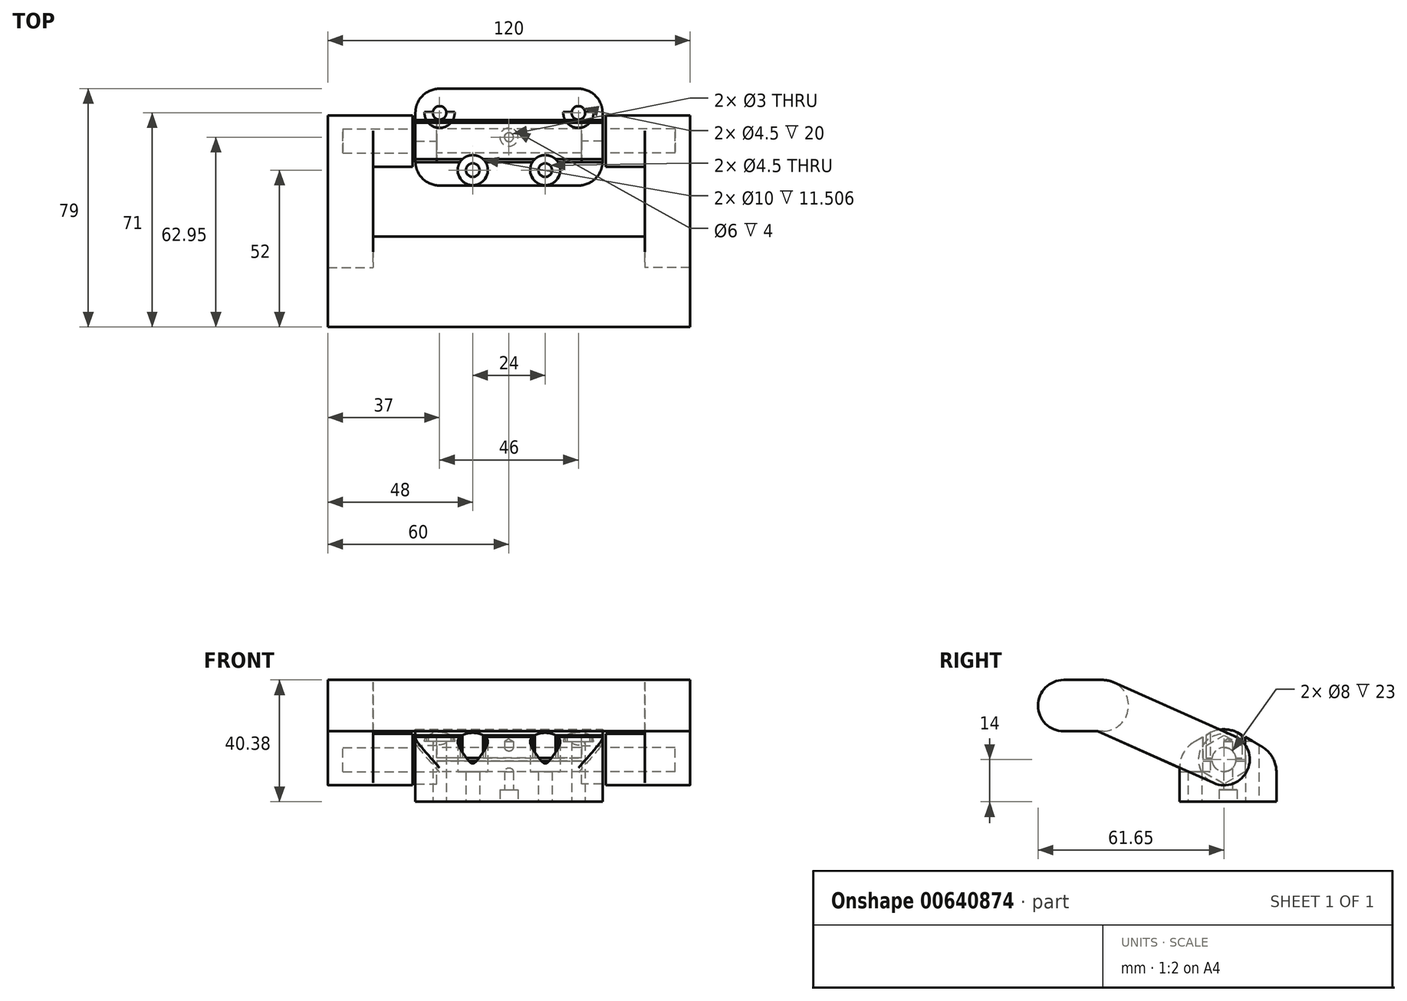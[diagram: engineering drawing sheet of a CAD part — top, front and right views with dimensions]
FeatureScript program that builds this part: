
annotation { "Feature Type Name" : "Feature", "Feature Type Description" : "" }
export const myFeature = defineFeature(function(context is Context, id is Id, definition is map)
    precondition{}
    {
        {
            var Q0;
            Q0=qCreatedBy(makeId("Top.planeOp"),FACE);
            var sketch = newSketch(context, id + "F0", { "sketchPlane" : qUnion([Q0])});
            skLineSegment(sketch, "E0.top", {"start": v(-31, -41) * mm, "end": v(31, -41) * mm, "construction": true});
            skLineSegment(sketch, "E0.left", {"start": v(-31, 41) * mm, "end": v(-31, -41) * mm, "construction": true});
            skLineSegment(sketch, "E0.right", {"start": v(31, 41) * mm, "end": v(31, -41) * mm, "construction": true});
            skPoint(sketch, "E0.middle", {"position": v(0, 0) * mm});
            skCircle(sketch, "E1", {"center": v(-23, 30) * mm, "radius": 2.25 * mm});
            skCircle(sketch, "E2", {"center": v(23, 30) * mm, "radius": 2.25 * mm});
            skCircle(sketch, "E3", {"center": v(-12, 11) * mm, "radius": 2.25 * mm});
            skCircle(sketch, "E4", {"center": v(12, 11) * mm, "radius": 2.25 * mm});
            skArc(sketch, "E5", {"start": v(-23, 38) * mm, "mid": v(-28.66, 35.66) * mm, "end": v(-31, 30) * mm});
            skArc(sketch, "E6", {"start": v(31, 30) * mm, "mid": v(28.66, 35.66) * mm, "end": v(23, 38) * mm});
            skCircle(sketch, "E7", {"center": v(12, 11) * mm, "radius": 5 * mm});
            skCircle(sketch, "E8", {"center": v(-12, 11) * mm, "radius": 5 * mm});
            skLineSegment(sketch, "E9", {"start": v(0, 41) * mm, "end": v(0, -41) * mm, "construction": true});
            skLineSegment(sketch, "E10", {"start": v(-31, 41) * mm, "end": v(31, 41) * mm, "construction": true});
            skLineSegment(sketch, "E11", {"start": v(-31, 38) * mm, "end": v(31, 38) * mm, "construction": true});
            skLineSegment(sketch, "E12", {"start": v(-23, 38) * mm, "end": v(23, 38) * mm});
            skLineSegment(sketch, "E13", {"start": v(23, 5.9) * mm, "end": v(-23, 5.9) * mm});
            skLineSegment(sketch, "E14", {"start": v(31, 30) * mm, "end": v(31, 13.9) * mm});
            skLineSegment(sketch, "E15", {"start": v(-31, 30) * mm, "end": v(-31, 13.9) * mm});
            skArc(sketch, "E16", {"start": v(23, 5.9) * mm, "mid": v(28.66, 8.24) * mm, "end": v(31, 13.9) * mm});
            skArc(sketch, "E17", {"start": v(-31, 13.9) * mm, "mid": v(-28.66, 8.24) * mm, "end": v(-23, 5.9) * mm});
            skLineSegment(sketch, "E18", {"start": v(-31, 20.65) * mm, "end": v(31, 20.65) * mm, "construction": true});
            skLineSegment(sketch, "E19.bottom", {"start": v(31, 27.65) * mm, "end": v(24, 27.65) * mm, "construction": true});
            skLineSegment(sketch, "E19.top", {"start": v(31, 13.65) * mm, "end": v(24, 13.65) * mm, "construction": true});
            skLineSegment(sketch, "E19.left", {"start": v(31, 27.65) * mm, "end": v(31, 13.65) * mm, "construction": true});
            skLineSegment(sketch, "E19.right", {"start": v(24, 27.65) * mm, "end": v(24, 13.65) * mm, "construction": true});
            skLineSegment(sketch, "E20.bottom", {"start": v(-31, 13.65) * mm, "end": v(-24, 13.65) * mm, "construction": true});
            skLineSegment(sketch, "E20.top", {"start": v(-31, 27.65) * mm, "end": v(-24, 27.65) * mm, "construction": true});
            skLineSegment(sketch, "E20.left", {"start": v(-31, 13.65) * mm, "end": v(-31, 27.65) * mm, "construction": true});
            skLineSegment(sketch, "E20.right", {"start": v(-24, 13.65) * mm, "end": v(-24, 27.65) * mm, "construction": true});
            skLineSegment(sketch, "E21", {"start": v(0, 38) * mm, "end": v(0, 5.9) * mm});
            skCircle(sketch, "E22", {"center": v(-23, 30) * mm, "radius": 5 * mm});
            skCircle(sketch, "E23", {"center": v(23, 30) * mm, "radius": 5 * mm});
            skPoint(sketch, "E24", {"position": v(0, 21.95) * mm});
            skSolve(sketch);
        }
        {
            var Q0;
            Q0=qCreatedBy(makeId("Right.planeOp"),FACE);
            var sketch = newSketch(context, id + "F1", { "sketchPlane" : qUnion([Q0])});
            skCircle(sketch, "E25", {"center": v(20.65, 14) * mm, "radius": 4 * mm});
            skLineSegment(sketch, "E26.bottom", {"start": v(5.9, 0) * mm, "end": v(38, 0) * mm});
            skLineSegment(sketch, "E27", {"start": v(20.65, 0) * mm, "end": v(20.65, 24) * mm, "construction": true});
            skCircle(sketch, "E28.cCircle", {"center": v(20.65, 14) * mm, "radius": 7 * mm, "construction": true});
            skLineSegment(sketch, "E28.0", {"start": v(13.65, 9.96) * mm, "end": v(13.65, 18.04) * mm});
            skLineSegment(sketch, "E28.1", {"start": v(13.65, 18.04) * mm, "end": v(20.65, 22.08) * mm});
            skLineSegment(sketch, "E28.2", {"start": v(20.65, 22.08) * mm, "end": v(27.65, 18.04) * mm});
            skLineSegment(sketch, "E28.3", {"start": v(27.65, 18.04) * mm, "end": v(27.65, 9.96) * mm});
            skLineSegment(sketch, "E28.4", {"start": v(27.65, 9.96) * mm, "end": v(20.65, 5.92) * mm});
            skLineSegment(sketch, "E28.5", {"start": v(20.65, 5.92) * mm, "end": v(13.65, 9.96) * mm});
            skPoint(sketch, "E28.0.midPoint", {"position": v(13.65, 14) * mm});
            skLineSegment(sketch, "E29", {"start": v(10.9, 19.92) * mm, "end": v(15.65, 22.66) * mm});
            skLineSegment(sketch, "E30", {"start": v(25.65, 22.66) * mm, "end": v(33, 18.42) * mm});
            skLineSegment(sketch, "E31", {"start": v(5.9, 11.26) * mm, "end": v(5.9, 0) * mm});
            skLineSegment(sketch, "E32", {"start": v(38, 0) * mm, "end": v(38, 9.76) * mm});
            skArc(sketch, "E33.filletArc", {"start": v(10.9, 19.92) * mm, "mid": v(7.24, 16.26) * mm, "end": v(5.9, 11.26) * mm});
            skArc(sketch, "E34.filletArc", {"start": v(25.65, 22.66) * mm, "mid": v(20.65, 24) * mm, "end": v(15.65, 22.66) * mm});
            skArc(sketch, "E35.filletArc", {"start": v(38, 9.76) * mm, "mid": v(36.66, 14.76) * mm, "end": v(33, 18.42) * mm});
            skSolve(sketch);
        }
        {
            var Q0;
            Q0=makeQuery(id+"F0.imprint","IMPRINT",FACE,{"disambiguationData":[TD([[makeQuery(id+"F0.imprint","IMPRINT",EDGE,{"derivedFrom":sQuery(id+"F0.wireOp",EDGE,"E2")}),-1.0]])]});
            var Q1;
            Q1=makeQuery(id+"F0.imprint","IMPRINT",FACE,{"disambiguationData":[TD([[makeQuery(id+"F0.imprint","IMPRINT",EDGE,{"derivedFrom":sQuery(id+"F0.wireOp",EDGE,"E7")}),-1.0]])]});
            var Q2;
            Q2=makeQuery(id+"F0.imprint","IMPRINT",FACE,{"disambiguationData":[TD([[makeQuery(id+"F0.imprint","IMPRINT",EDGE,{"derivedFrom":sQuery(id+"F0.wireOp",EDGE,"E4")}),-1.0]])]});
            var Q3;
            Q3=sQuery(id+"F1.wireOp",VERTEX,"yncq1Wx2-fRUI-TJXd-Kln3-WqJ49cqU4spt.right.start");
            extrude(context, id + "F2", {"entities" : qUnion([Q0, Q1, Q2]), "depth" : 10 * mm, "endBoundEntityVertex" : qUnion([Q3]), "offsetDistance" : 25 * mm});
        }
        {
            var Q0;
            {var subQ1=sQuery(id+"F0.wireOp",EDGE,"E6");Q0=makeQuery(id+"F0.imprint","IMPRINT",FACE,{"disambiguationData":[TD([[makeQuery(id+"F0.imprint","IMPRINT",EDGE,{"derivedFrom":subQ1}),1.0]])]});}
            var Q1;
            Q1=makeQuery(id+"F0.imprint","IMPRINT",FACE,{"disambiguationData":[TD([[makeQuery(id+"F0.imprint","IMPRINT",EDGE,{"derivedFrom":sQuery(id+"F0.wireOp",EDGE,"E2")}),-1.0]])]});
            extrude(context, id + "F3", {"entities" : qUnion([Q0, Q1]), "operationType" : NewBodyOperationType.ADD, "depth" : 20 * mm, "offsetDistance" : 25 * mm});
        }
        {
            var Q0;
            Q0=makeQuery(id+"F0.imprint","IMPRINT",FACE,{"disambiguationData":[TD([[makeQuery(id+"F0.imprint","IMPRINT",EDGE,{"derivedFrom":sQuery(id+"F0.wireOp",EDGE,"E7")}),-1.0]])]});
            var Q1;
            Q1=sQuery(id+"F1.wireOp",VERTEX,"E27.end");
            extrude(context, id + "F4", {"entities" : qUnion([Q0]), "operationType" : NewBodyOperationType.ADD, "endBound" : BoundingType.UP_TO_VERTEX, "depth" : 25 * mm, "endBoundEntityVertex" : qUnion([Q1]), "offsetDistance" : 25 * mm});
        }
        {
            var Q0;
            Q0=makeQuery(id+"F1.imprint","IMPRINT",FACE,{"disambiguationData":[TD([[makeQuery(id+"F1.imprint","IMPRINT",EDGE,{"derivedFrom":sQuery(id+"F1.wireOp",EDGE,"E25")}),1.0]])]});
            extrude(context, id + "F5", {"entities" : qUnion([Q0]), "operationType" : NewBodyOperationType.REMOVE, "endBound" : BoundingType.THROUGH_ALL, "depth" : 25 * mm, "offsetDistance" : 25 * mm, "hasSecondDirection" : true, "secondDirectionOppositeDirection" : false, "secondDirectionDepth" : 10 * mm});
        }
        {
            var Q0;
            Q0=sQuery(id+"F0.wireOp",VERTEX,"E24");
            var Q1;
            Q1=makeQuery(id+"F2.opExtrude","SWEPT_BODY",BODY,{"disambiguationData":[OSD([sQuery(id+"F0.wireOp",EDGE,"E2"),sQuery(id+"F0.wireOp",EDGE,"E4"),sQuery(id+"F0.wireOp",EDGE,"E6"),sQuery(id+"F0.wireOp",EDGE,"E12"),sQuery(id+"F0.wireOp",EDGE,"E13"),sQuery(id+"F0.wireOp",EDGE,"E14"),sQuery(id+"F0.wireOp",EDGE,"E16"),sQuery(id+"F0.wireOp",EDGE,"E21")])]});
            hole(context, id + "F6", {"style" : HoleStyle.C_BORE, "endStyle" : HoleEndStyle.BLIND, "oppositeDirection" : true, "holeDiameter" : 3 * mm, "cBoreDiameter" : 6 * mm, "cBoreDepth" : 4 * mm, "majorDiameter" : 5 * mm, "holeDepth" : 20 * mm, "isTappedThrough" : true, "tappedDepth" : 12 * mm, "tapClearance" : 3, "locations" : qUnion([Q0]), "scope" : qUnion([Q1])});
        }
        {
            var Q0;
            Q0=makeQuery(id+"F1.imprint","IMPRINT",FACE,{"disambiguationData":[TD([[makeQuery(id+"F1.imprint","IMPRINT",EDGE,{"derivedFrom":sQuery(id+"F1.wireOp",EDGE,"E28.0")}),1.0]])]});
            var Q1;
            Q1=makeQuery(id+"F1.imprint","IMPRINT",FACE,{"disambiguationData":[TD([[makeQuery(id+"F1.imprint","IMPRINT",EDGE,{"derivedFrom":sQuery(id+"F1.wireOp",EDGE,"E25")}),-1.0]])]});
            var Q2;
            Q2=makeQuery(id+"F1.imprint","IMPRINT",FACE,{"disambiguationData":[TD([[makeQuery(id+"F1.imprint","IMPRINT",EDGE,{"derivedFrom":sQuery(id+"F1.wireOp",EDGE,"E25")}),1.0]])]});
            extrude(context, id + "F7", {"entities" : qUnion([Q0, Q1, Q2]), "operationType" : NewBodyOperationType.INTERSECT, "endBound" : BoundingType.THROUGH_ALL, "oppositeDirection" : true, "depth" : 25 * mm, "offsetDistance" : 25 * mm, "hasSecondDirection" : true, "secondDirectionBound" : SecondDirectionBoundingType.THROUGH_ALL, "secondDirectionOppositeDirection" : false, "secondDirectionDepth" : 25 * mm});
        }
        {
            var Q0;
            Q0=makeQuery(id+"F1.imprint","IMPRINT",FACE,{"disambiguationData":[TD([[makeQuery(id+"F1.imprint","IMPRINT",EDGE,{"derivedFrom":sQuery(id+"F1.wireOp",EDGE,"E25")}),-1.0]])]});
            var Q1;
            Q1=sQuery(id+"F0.wireOp",VERTEX,"E10.end");
            var Q2;
            Q2=sQuery(id+"F0.wireOp",VERTEX,"E19.right.end");
            extrude(context, id + "F8", {"entities" : qUnion([Q0]), "operationType" : NewBodyOperationType.REMOVE, "endBound" : BoundingType.UP_TO_VERTEX, "depth" : 25 * mm, "endBoundEntityVertex" : qUnion([Q1]), "offsetDistance" : 25 * mm, "hasSecondDirection" : true, "secondDirectionBound" : SecondDirectionBoundingType.UP_TO_VERTEX, "secondDirectionOppositeDirection" : false, "secondDirectionDepth" : 25 * mm, "secondDirectionBoundEntityVertex" : qUnion([Q2])});
        }
        {
            var Q0;
            {var subQ0=sQuery(id+"F0.wireOp",EDGE,"E14");Q0=makeQuery(id+"F4.boolean.opBoolean","MERGE",FACE,{"derivedFrom":[makeQuery(id+"F3.boolean.opBoolean","MERGE",FACE,{"derivedFrom":[makeQuery(id+"F2.opExtrude","SWEPT_FACE",FACE,{"disambiguationData":[OSD([subQ0])]}),makeQuery(id+"F3.opExtrude","SWEPT_FACE",FACE,{"disambiguationData":[OSD([subQ0])]})]}),makeQuery(id+"F4.opExtrude","SWEPT_FACE",FACE,{"disambiguationData":[OSD([subQ0])]})]});}
            var sketch = newSketch(context, id + "F9", { "sketchPlane" : qUnion([Q0])});
            skLineSegment(sketch, "E36.bottom", {"start": v(13.65, 13.5) * mm, "end": v(27.65, 13.5) * mm});
            skLineSegment(sketch, "E36.left", {"start": v(13.65, 21.5) * mm, "end": v(13.65, 13.5) * mm});
            skLineSegment(sketch, "E36.right", {"start": v(27.65, 21.5) * mm, "end": v(27.65, 13.5) * mm});
            skLineSegment(sketch, "E37.bottom", {"start": v(14.65, 14.5) * mm, "end": v(26.65, 14.5) * mm});
            skLineSegment(sketch, "E37.left", {"start": v(14.65, 22.08) * mm, "end": v(14.65, 14.5) * mm});
            skLineSegment(sketch, "E37.right", {"start": v(26.65, 22.08) * mm, "end": v(26.65, 14.5) * mm});
            skLineSegment(sketch, "E38", {"start": v(20.65, 22.08) * mm, "end": v(20.65, 5.92) * mm, "construction": true});
            skLineSegment(sketch, "E39", {"start": v(13.65, 14) * mm, "end": v(27.65, 14) * mm, "construction": true});
            skLineSegment(sketch, "E40", {"start": v(13.65, 21.5) * mm, "end": v(14.65, 22.08) * mm});
            skLineSegment(sketch, "E41", {"start": v(26.65, 22.08) * mm, "end": v(27.65, 21.5) * mm});
            skSolve(sketch);
        }
        {
            var Q0;
            {var subQ4=sQuery(id+"F9.wireOp",EDGE,"E36.bottom");Q0=makeQuery(id+"F9.imprint","IMPRINT",FACE,{"disambiguationData":[TD([[makeQuery(id+"F9.imprint","IMPRINT",EDGE,{"derivedFrom":subQ4}),1.0]])]});}
            var Q1;
            {var subQ3=sQuery(id+"F9.wireOp",EDGE,"E40");Q1=makeQuery(id+"F9.imprint","IMPRINT",FACE,{"disambiguationData":[TD([[makeQuery(id+"F9.imprint","IMPRINT",EDGE,{"derivedFrom":subQ3}),-1.0]])]});}
            var Q2;
            {var subQ3=sQuery(id+"F9.wireOp",EDGE,"E41");Q2=makeQuery(id+"F9.imprint","IMPRINT",FACE,{"disambiguationData":[TD([[makeQuery(id+"F9.imprint","IMPRINT",EDGE,{"derivedFrom":subQ3}),-1.0]])]});}
            extrude(context, id + "F10", {"entities" : qUnion([Q0, Q1, Q2]), "operationType" : NewBodyOperationType.REMOVE, "endBound" : BoundingType.THROUGH_ALL, "oppositeDirection" : true, "depth" : 25 * mm, "offsetDistance" : 25 * mm});
        }
        {
            var Q0;
            Q0=qCreatedBy(makeId("Right.planeOp"),FACE);
            var sketch = newSketch(context, id + "F11", { "sketchPlane" : qUnion([Q0])});
            skLineSegment(sketch, "E42.bottom", {"start": v(41, 40.38) * mm, "end": v(-41, 40.38) * mm, "construction": true});
            skLineSegment(sketch, "E42.left", {"start": v(41, 40.38) * mm, "end": v(41, 0) * mm, "construction": true});
            skLineSegment(sketch, "E42.right", {"start": v(-41, 40.38) * mm, "end": v(-41, 0) * mm, "construction": true});
            skLineSegment(sketch, "E43", {"start": v(-19.5, 40.38) * mm, "end": v(-32.5, 40.38) * mm});
            skLineSegment(sketch, "E44", {"start": v(-19.5, 23.38) * mm, "end": v(-32.5, 23.38) * mm});
            skArc(sketch, "E45.trimOffspring", {"start": v(-19.5, 23.38) * mm, "mid": v(-11, 31.88) * mm, "end": v(-19.5, 40.38) * mm});
            skArc(sketch, "E46.trimOffspring", {"start": v(-32.5, 40.38) * mm, "mid": v(-41, 31.88) * mm, "end": v(-32.5, 23.38) * mm});
            skLineSegment(sketch, "E47", {"start": v(-16.04, 39.64) * mm, "end": v(24.1, 21.77) * mm});
            skLineSegment(sketch, "E48", {"start": v(17.2, 6.23) * mm, "end": v(-21.3, 23.38) * mm});
            skLineSegment(sketch, "E49", {"start": v(20.65, 14) * mm, "end": v(-19.5, 31.88) * mm, "construction": true});
            skLineSegment(sketch, "E50", {"start": v(-19.5, 31.88) * mm, "end": v(-32.5, 31.88) * mm, "construction": true});
            skArc(sketch, "E51", {"start": v(-19.5, 40.38) * mm, "mid": v(-28, 31.88) * mm, "end": v(-19.5, 23.38) * mm, "construction": true});
            skArc(sketch, "E52", {"start": v(17.2, 6.23) * mm, "mid": v(28.42, 10.54) * mm, "end": v(24.1, 21.77) * mm});
            skCircle(sketch, "E53", {"center": v(20.65, 14) * mm, "radius": 4 * mm});
            skArc(sketch, "E54", {"start": v(24.1, 21.77) * mm, "mid": v(12.88, 17.46) * mm, "end": v(17.2, 6.23) * mm});
            skSolve(sketch);
        }
        {
            var Q0;
            {var subQ6=sQuery(id+"F11.wireOp",EDGE,"E43");Q0=makeQuery(id+"F11.imprint","IMPRINT",FACE,{"disambiguationData":[TD([[makeQuery(id+"F11.imprint","IMPRINT",EDGE,{"derivedFrom":subQ6}),1.0]])]});}
            extrude(context, id + "F12", {"entities" : qUnion([Q0]), "depth" : 60 * mm, "offsetDistance" : 25 * mm});
        }
        {
            var Q0;
            {var subQ4=sQuery(id+"F11.wireOp",EDGE,"E47");Q0=makeQuery(id+"F11.imprint","IMPRINT",FACE,{"disambiguationData":[TD([[makeQuery(id+"F11.imprint","IMPRINT",EDGE,{"derivedFrom":subQ4}),-1.0]])]});}
            var Q1;
            Q1=makeQuery(id+"F11.imprint","IMPRINT",FACE,{"disambiguationData":[TD([[makeQuery(id+"F11.imprint","IMPRINT",EDGE,{"derivedFrom":sQuery(id+"F11.wireOp",EDGE,"E52")}),1.0]])]});
            var Q2;
            Q2=makeQuery(id+"F11.imprint","IMPRINT",FACE,{"disambiguationData":[TD([[makeQuery(id+"F11.imprint","IMPRINT",EDGE,{"derivedFrom":sQuery(id+"F11.wireOp",EDGE,"E53")}),1.0]])]});
            extrude(context, id + "F13", {"entities" : qUnion([Q0, Q1, Q2]), "operationType" : NewBodyOperationType.ADD, "depth" : (45 + 15) * mm, "offsetDistance" : 25 * mm, "hasSecondDirection" : true, "secondDirectionOppositeDirection" : false, "secondDirectionDepth" : 45 * mm});
        }
        {
            var Q0;
            Q0=makeQuery(id+"F11.imprint","IMPRINT",FACE,{"disambiguationData":[TD([[makeQuery(id+"F11.imprint","IMPRINT",EDGE,{"derivedFrom":sQuery(id+"F11.wireOp",EDGE,"E52")}),1.0]])]});
            var Q1;
            Q1=makeQuery(id+"F11.imprint","IMPRINT",FACE,{"disambiguationData":[TD([[makeQuery(id+"F11.imprint","IMPRINT",EDGE,{"derivedFrom":sQuery(id+"F11.wireOp",EDGE,"E53")}),1.0]])]});
            var Q2;
            Q2=makeQuery(id+"F13.opExtrude","CAP_FACE",FACE,{"disambiguationData":[OSD([sQuery(id+"F11.wireOp",EDGE,"E43"),sQuery(id+"F11.wireOp",EDGE,"E44"),sQuery(id+"F11.wireOp",EDGE,"E45.trimOffspring"),sQuery(id+"F11.wireOp",EDGE,"E46.trimOffspring"),sQuery(id+"F11.wireOp",EDGE,"E47"),sQuery(id+"F11.wireOp",EDGE,"E48"),sQuery(id+"F11.wireOp",EDGE,"E52")])],"isStart":true});
            extrude(context, id + "F14", {"entities" : qUnion([Q0, Q1]), "operationType" : NewBodyOperationType.ADD, "endBound" : BoundingType.UP_TO_SURFACE, "depth" : 25 * mm, "endBoundEntityFace" : qUnion([Q2]), "offsetDistance" : 25 * mm, "hasSecondDirection" : true, "secondDirectionOppositeDirection" : false, "secondDirectionDepth" : 32 * mm});
        }
        {
            var Q0;
            Q0=makeQuery(id+"F11.imprint","IMPRINT",FACE,{"disambiguationData":[TD([[makeQuery(id+"F11.imprint","IMPRINT",EDGE,{"derivedFrom":sQuery(id+"F11.wireOp",EDGE,"E53")}),1.0]])]});
            extrude(context, id + "F15", {"entities" : qUnion([Q0]), "operationType" : NewBodyOperationType.REMOVE, "depth" : 55 * mm, "offsetDistance" : 25 * mm});
        }
        {
            var Q0;
            Q0=makeQuery(id+"F12.opExtrude","SWEPT_BODY",BODY,{"disambiguationData":[OSD([sQuery(id+"F11.wireOp",EDGE,"E43"),sQuery(id+"F11.wireOp",EDGE,"E44"),sQuery(id+"F11.wireOp",EDGE,"E45.trimOffspring"),sQuery(id+"F11.wireOp",EDGE,"E46.trimOffspring")])]});
            var Q1;
            Q1=makeQuery(id+"F2.opExtrude","SWEPT_BODY",BODY,{"disambiguationData":[OSD([sQuery(id+"F0.wireOp",EDGE,"E1"),sQuery(id+"F0.wireOp",EDGE,"E2"),sQuery(id+"F0.wireOp",EDGE,"E3"),sQuery(id+"F0.wireOp",EDGE,"E4"),sQuery(id+"F0.wireOp",EDGE,"E5"),sQuery(id+"F0.wireOp",EDGE,"E6"),sQuery(id+"F0.wireOp",EDGE,"E12"),sQuery(id+"F0.wireOp",EDGE,"E13"),sQuery(id+"F0.wireOp",EDGE,"E14"),sQuery(id+"F0.wireOp",EDGE,"E15"),sQuery(id+"F0.wireOp",EDGE,"E16"),sQuery(id+"F0.wireOp",EDGE,"E17")])]});
            var Q2;
            {var subQ6=sQuery(id+"F11.wireOp",EDGE,"E43");Q2=makeQuery(id+"F11.imprint","IMPRINT",FACE,{"disambiguationData":[TD([[makeQuery(id+"F11.imprint","IMPRINT",EDGE,{"derivedFrom":subQ6}),1.0]])]});}
            mirror(context, id + "F16", {"operationType" : NewBodyOperationType.ADD, "entities" : qUnion([Q0, Q1]), "mirrorPlane" : qUnion([Q2])});
        }
    });
